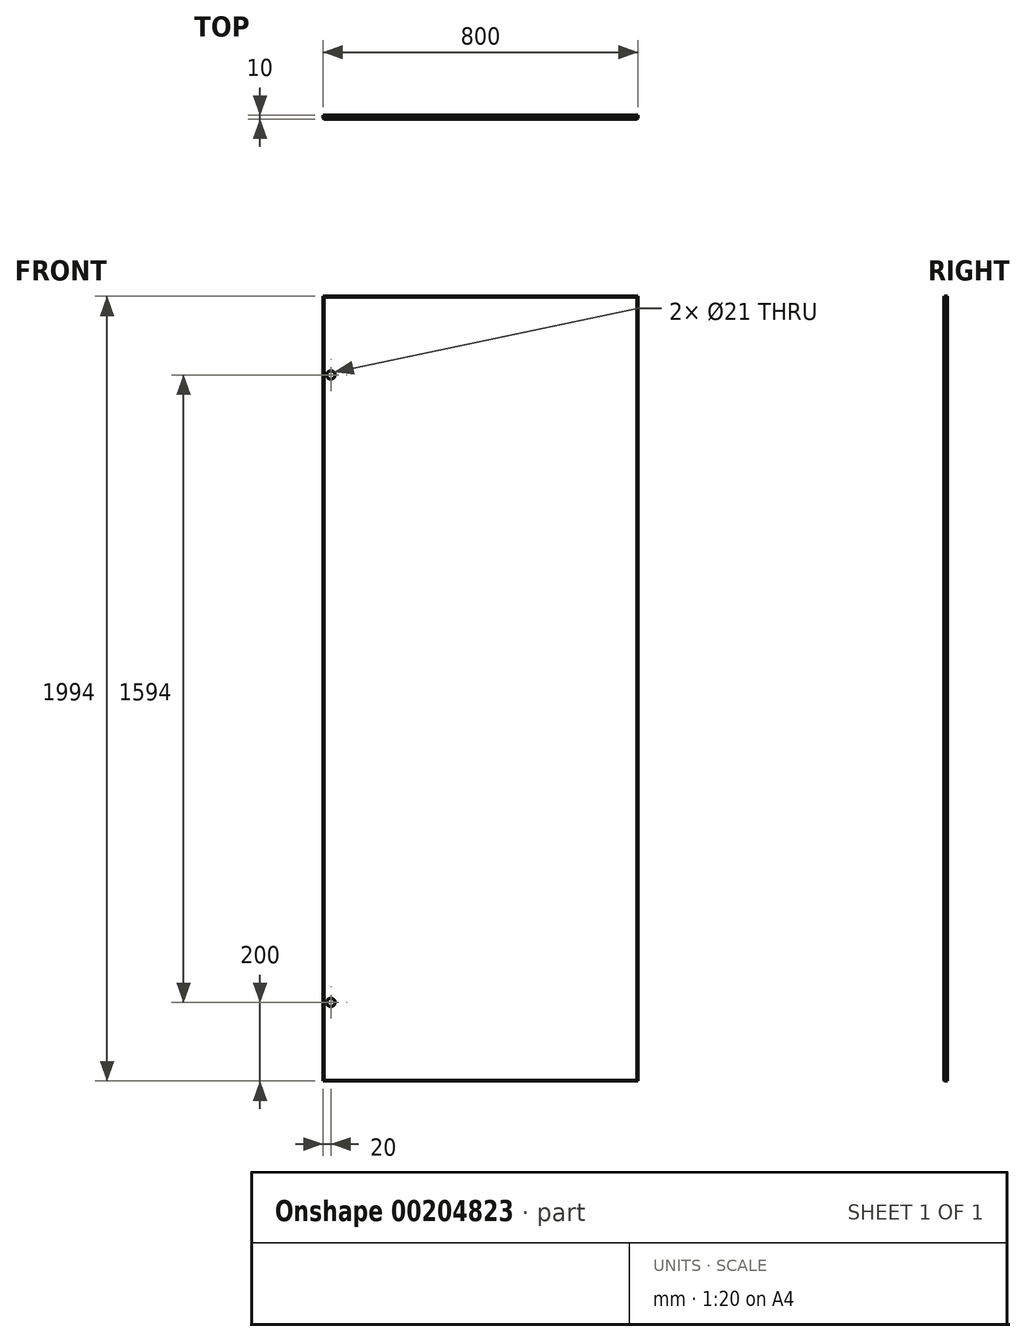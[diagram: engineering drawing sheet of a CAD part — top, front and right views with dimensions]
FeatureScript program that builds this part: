
annotation { "Feature Type Name" : "Feature", "Feature Type Description" : "" }
export const myFeature = defineFeature(function(context is Context, id is Id, definition is map)
    precondition{}
    {
        {
            var Q0;
            Q0=qCreatedBy(makeId("Front.planeOp"),FACE);
            var sketch = newSketch(context, id + "F0", { "sketchPlane" : qUnion([Q0])});
            skLineSegment(sketch, "E0.bottom", {"start": v(0, 0) * mm, "end": v(800, 0) * mm});
            skLineSegment(sketch, "E0.top", {"start": v(0, 1994) * mm, "end": v(800, 1994) * mm});
            skLineSegment(sketch, "E0.left", {"start": v(0, 0) * mm, "end": v(0, 1994) * mm});
            skLineSegment(sketch, "E0.right", {"start": v(800, 0) * mm, "end": v(800, 1994) * mm});
            skSolve(sketch);
        }
        {
            var Q0;
            Q0=makeQuery(id+"F0.imprint","IMPRINT",FACE,{"disambiguationData":[TD([[makeQuery(id+"F0.imprint","IMPRINT",EDGE,{"derivedFrom":sQuery(id+"F0.wireOp",EDGE,"E0.bottom")}),1.0]])]});
            extrude(context, id + "F1", {"entities" : qUnion([Q0]), "depth" : 10 * mm});
        }
        {
            var Q0;
            Q0=makeQuery(id+"F1.opExtrude","CAP_FACE",FACE,{"disambiguationData":[OSD([sQuery(id+"F0.wireOp",EDGE,"E0.bottom"),sQuery(id+"F0.wireOp",EDGE,"E0.top"),sQuery(id+"F0.wireOp",EDGE,"E0.left"),sQuery(id+"F0.wireOp",EDGE,"E0.right")])],"isStart":false});
            chamfer(context, id + "F2", {"entities" : qUnion([Q0]), "width" : 2 * mm, "tangentPropagation" : true});
        }
        {
            var Q0;
            Q0=makeQuery(id+"F1.opExtrude","CAP_FACE",FACE,{"disambiguationData":[OSD([sQuery(id+"F0.wireOp",EDGE,"E0.bottom"),sQuery(id+"F0.wireOp",EDGE,"E0.top"),sQuery(id+"F0.wireOp",EDGE,"E0.left"),sQuery(id+"F0.wireOp",EDGE,"E0.right")])],"isStart":false});
            var sketch = newSketch(context, id + "F3", { "sketchPlane" : qUnion([Q0])});
            skCircle(sketch, "E1", {"center": v(20, 1794) * mm, "radius": 10.5 * mm});
            skCircle(sketch, "E2", {"center": v(20, 200) * mm, "radius": 10.5 * mm});
            skSolve(sketch);
        }
        {
            var Q0;
            Q0=makeQuery(id+"F3.imprint","IMPRINT",FACE,{"disambiguationData":[TD([[makeQuery(id+"F3.imprint","IMPRINT",EDGE,{"derivedFrom":sQuery(id+"F3.wireOp",EDGE,"E1")}),1.0]])]});
            var Q1;
            Q1=makeQuery(id+"F3.imprint","IMPRINT",FACE,{"disambiguationData":[TD([[makeQuery(id+"F3.imprint","IMPRINT",EDGE,{"derivedFrom":sQuery(id+"F3.wireOp",EDGE,"E2")}),1.0]])]});
            extrude(context, id + "F4", {"entities" : qUnion([Q0, Q1]), "operationType" : NewBodyOperationType.REMOVE, "oppositeDirection" : true, "depth" : 25 * mm});
        }
    });
